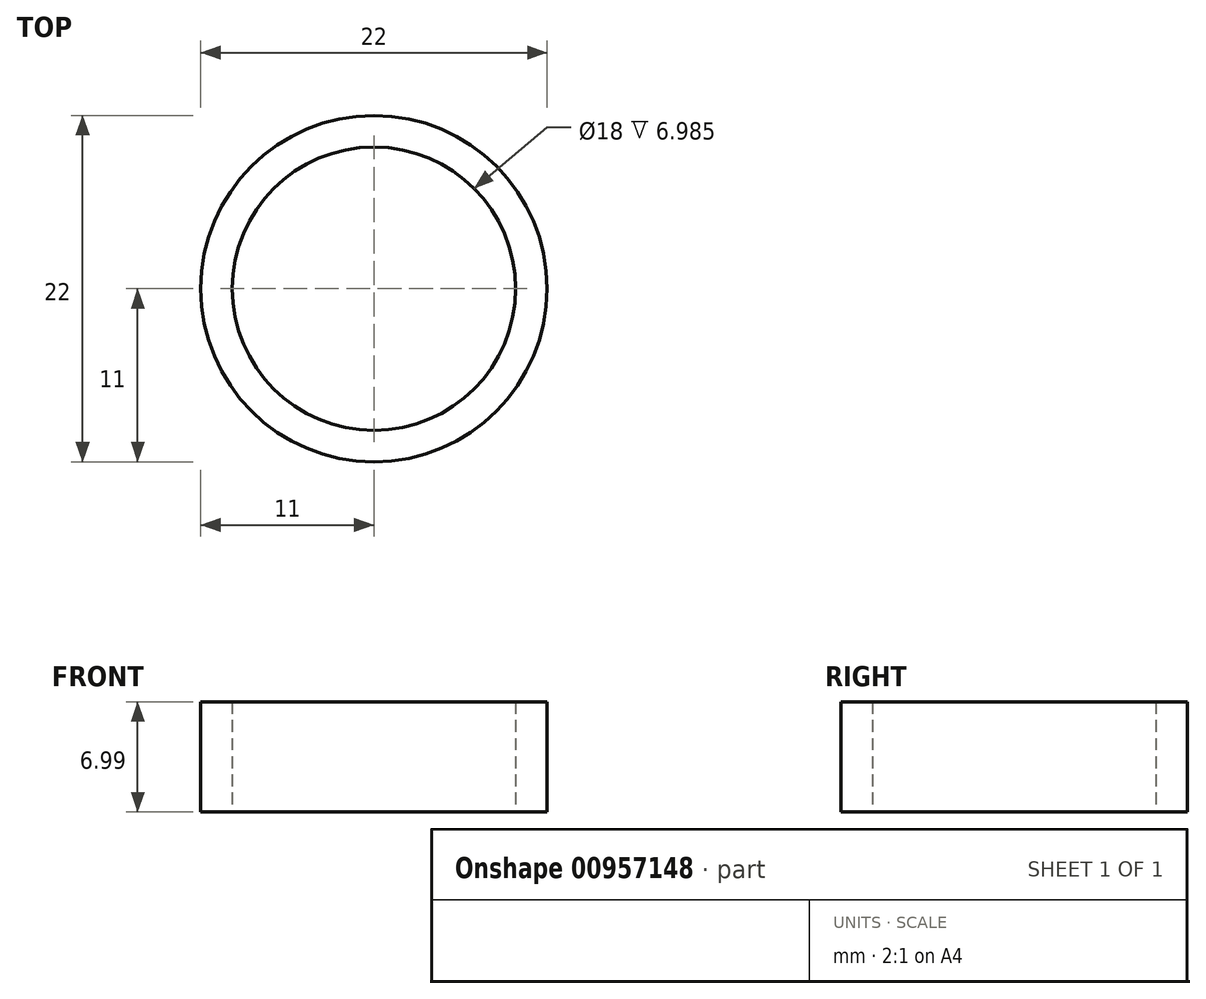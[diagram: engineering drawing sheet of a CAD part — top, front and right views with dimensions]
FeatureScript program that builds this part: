
annotation { "Feature Type Name" : "Feature", "Feature Type Description" : "" }
export const myFeature = defineFeature(function(context is Context, id is Id, definition is map)
    precondition{}
    {
        {
            var Q0;
            Q0=qCreatedBy(makeId("Top.planeOp"),FACE);
            var sketch = newSketch(context, id + "F0", { "sketchPlane" : qUnion([Q0])});
            skCircle(sketch, "E0", {"center": v(0, 0) * mm, "radius": 11 * mm});
            skCircle(sketch, "E1.0", {"center": v(0, 0) * mm, "radius": 9 * mm});
            skSolve(sketch);
        }
        {
            var Q0;
            Q0=makeQuery(id+"F0.imprint","IMPRINT",FACE,{"disambiguationData":[TD([[makeQuery(id+"F0.imprint","IMPRINT",EDGE,{"derivedFrom":sQuery(id+"F0.wireOp",EDGE,"E0")}),1.0]])]});
            extrude(context, id + "F1", {"entities" : qUnion([Q0]), "depth" : 7 * mm, "offsetDistance" : 25.4 * mm});
        }
    });
